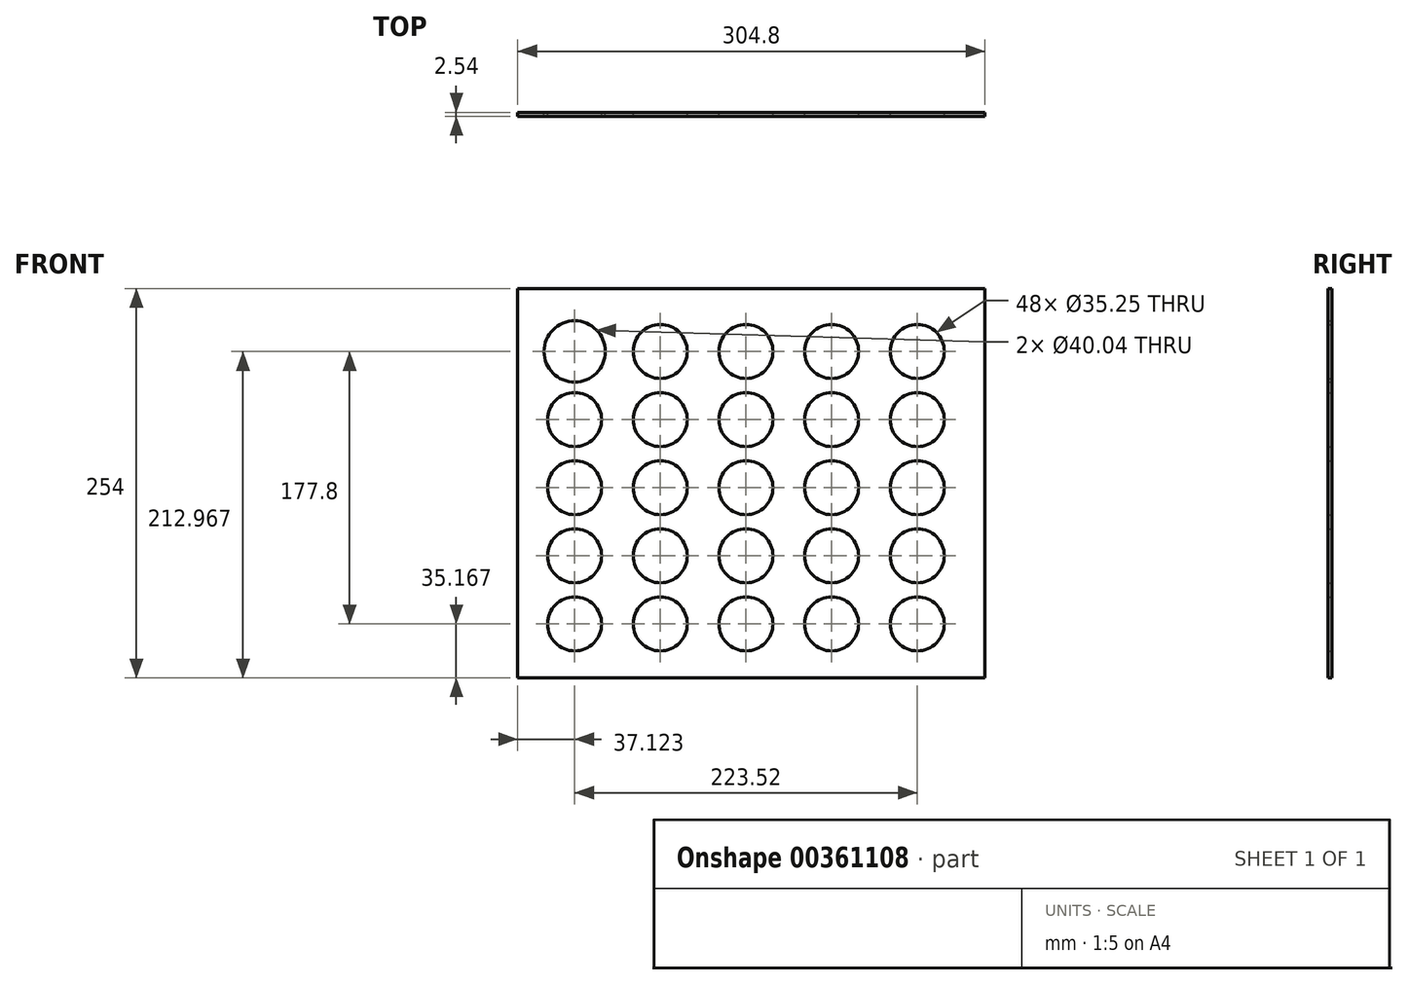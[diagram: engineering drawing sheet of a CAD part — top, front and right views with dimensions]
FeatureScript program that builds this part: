
annotation { "Feature Type Name" : "Feature", "Feature Type Description" : "" }
export const myFeature = defineFeature(function(context is Context, id is Id, definition is map)
    precondition{}
    {
        {
            var Q0;
            Q0=qCreatedBy(makeId("Front.planeOp"),FACE);
            var sketch = newSketch(context, id + "F0", { "sketchPlane" : qUnion([Q0])});
            skLineSegment(sketch, "E0.bottom", {"start": v(-105.95, 165.54) * mm, "end": v(198.85, 165.54) * mm});
            skLineSegment(sketch, "E0.top", {"start": v(-105.95, -88.46) * mm, "end": v(198.85, -88.46) * mm});
            skLineSegment(sketch, "E0.left", {"start": v(-105.95, 165.54) * mm, "end": v(-105.95, -88.46) * mm});
            skLineSegment(sketch, "E0.right", {"start": v(198.85, 165.54) * mm, "end": v(198.85, -88.46) * mm});
            skCircle(sketch, "E1", {"center": v(-68.83, 124.5) * mm, "radius": 20.02 * mm});
            skCircle(sketch, "E2", {"center": v(-68.83, 124.5) * mm, "radius": 17.62 * mm});
            skCircle(sketch, "E3.0.1.0", {"center": v(-68.83, 80.06) * mm, "radius": 17.62 * mm});
            skCircle(sketch, "E3.0.2.0", {"center": v(-68.83, 35.6) * mm, "radius": 17.62 * mm});
            skCircle(sketch, "E3.0.3.0", {"center": v(-68.83, -8.84) * mm, "radius": 17.62 * mm});
            skCircle(sketch, "E3.0.4.0", {"center": v(-68.83, -53.3) * mm, "radius": 17.62 * mm});
            skCircle(sketch, "E3.1.0.0", {"center": v(-12.95, 124.5) * mm, "radius": 17.62 * mm});
            skCircle(sketch, "E3.1.1.0", {"center": v(-12.95, 80.06) * mm, "radius": 17.62 * mm});
            skCircle(sketch, "E3.1.2.0", {"center": v(-12.95, 35.6) * mm, "radius": 17.62 * mm});
            skCircle(sketch, "E3.1.3.0", {"center": v(-12.95, -8.84) * mm, "radius": 17.62 * mm});
            skCircle(sketch, "E3.1.4.0", {"center": v(-12.95, -53.3) * mm, "radius": 17.62 * mm});
            skCircle(sketch, "E3.2.0.0", {"center": v(42.93, 124.5) * mm, "radius": 17.62 * mm});
            skCircle(sketch, "E3.2.1.0", {"center": v(42.93, 80.06) * mm, "radius": 17.62 * mm});
            skCircle(sketch, "E3.2.2.0", {"center": v(42.93, 35.6) * mm, "radius": 17.62 * mm});
            skCircle(sketch, "E3.2.3.0", {"center": v(42.93, -8.84) * mm, "radius": 17.62 * mm});
            skCircle(sketch, "E3.2.4.0", {"center": v(42.93, -53.3) * mm, "radius": 17.62 * mm});
            skCircle(sketch, "E3.3.0.0", {"center": v(98.81, 124.5) * mm, "radius": 17.62 * mm});
            skCircle(sketch, "E3.3.1.0", {"center": v(98.81, 80.06) * mm, "radius": 17.62 * mm});
            skCircle(sketch, "E3.3.2.0", {"center": v(98.81, 35.6) * mm, "radius": 17.62 * mm});
            skCircle(sketch, "E3.3.3.0", {"center": v(98.81, -8.84) * mm, "radius": 17.62 * mm});
            skCircle(sketch, "E3.3.4.0", {"center": v(98.81, -53.3) * mm, "radius": 17.62 * mm});
            skCircle(sketch, "E3.4.0.0", {"center": v(154.7, 124.5) * mm, "radius": 17.62 * mm});
            skCircle(sketch, "E3.4.1.0", {"center": v(154.7, 80.06) * mm, "radius": 17.62 * mm});
            skCircle(sketch, "E3.4.2.0", {"center": v(154.7, 35.6) * mm, "radius": 17.62 * mm});
            skCircle(sketch, "E3.4.3.0", {"center": v(154.7, -8.84) * mm, "radius": 17.62 * mm});
            skCircle(sketch, "E3.4.4.0", {"center": v(154.7, -53.3) * mm, "radius": 17.62 * mm});
            skLineSegment(sketch, "E3.direction1", {"start": v(-68.83, 124.5) * mm, "end": v(-12.95, 124.5) * mm, "construction": true});
            skLineSegment(sketch, "E3.direction2", {"start": v(-68.83, 124.5) * mm, "end": v(-68.83, 80.06) * mm, "construction": true});
            skSolve(sketch);
        }
        {
            var Q0;
            Q0=qSketchRegion(id+"F0",true);
            extrude(context, id + "F1", {"entities" : qUnion([Q0]), "depth" : 2.54 * mm});
        }
        {
            var Q0;
            Q0=qSketchRegion(id+"F0",true);
            extrude(context, id + "F2", {"entities" : qUnion([Q0]), "depth" : 0.03 * mm});
        }
    });
